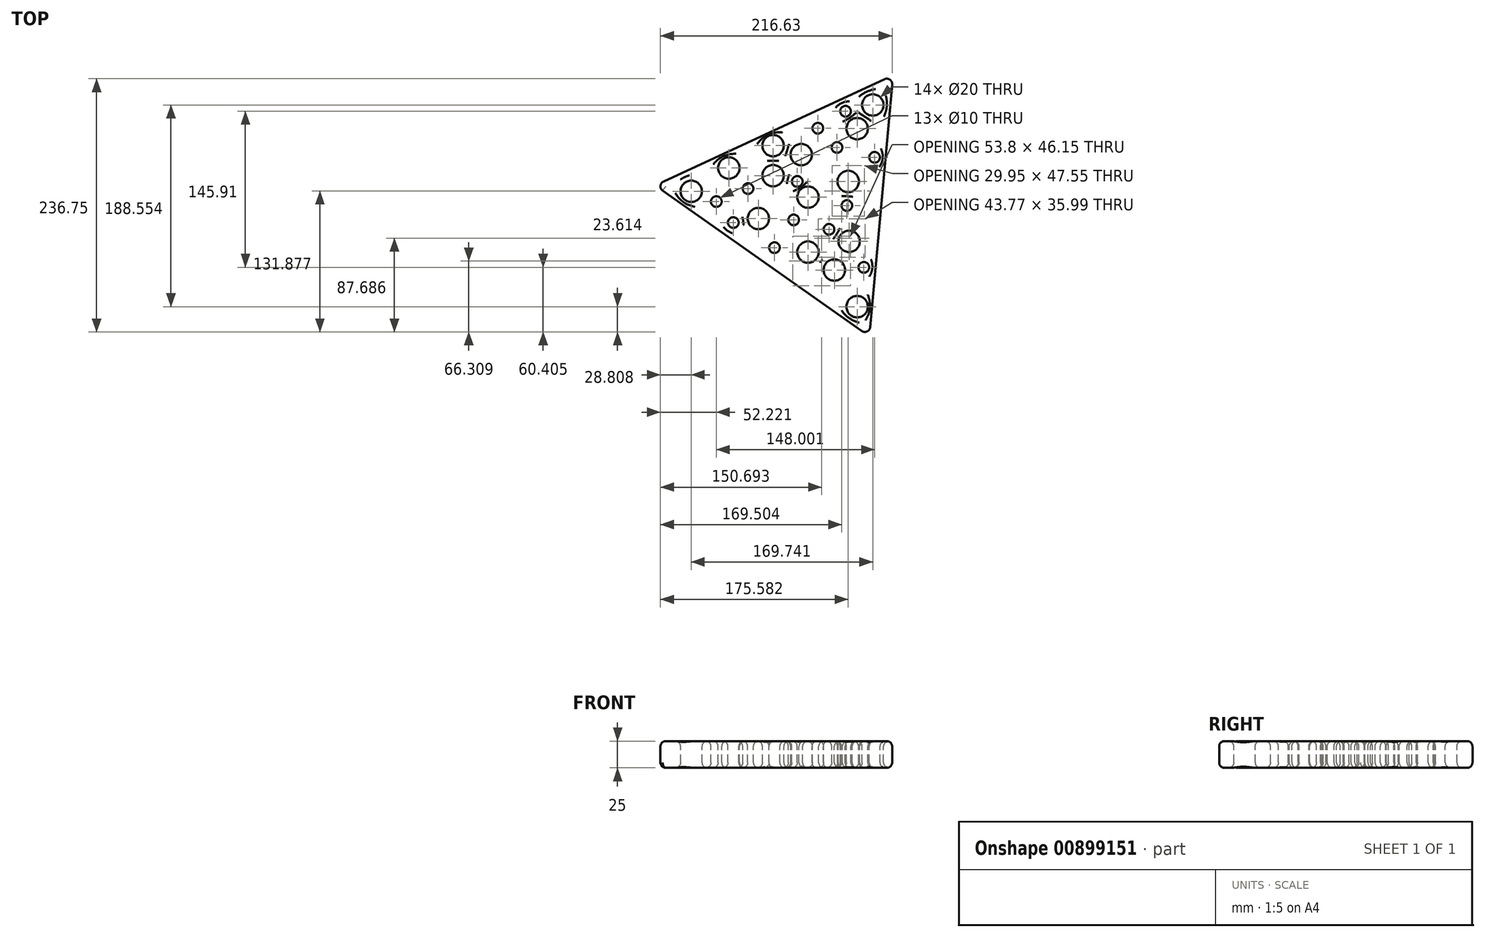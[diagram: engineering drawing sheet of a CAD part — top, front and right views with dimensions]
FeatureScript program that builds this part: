
annotation { "Feature Type Name" : "Feature", "Feature Type Description" : "" }
export const myFeature = defineFeature(function(context is Context, id is Id, definition is map)
    precondition{}
    {
        {
            var Q0;
            Q0=qCreatedBy(makeId("Top.planeOp"),FACE);
            var sketch = newSketch(context, id + "F0", { "sketchPlane" : qUnion([Q0])});
            skLineSegment(sketch, "E0", {"start": v(7.08, -4.99) * mm, "end": v(193.2, -136.12) * mm});
            skLineSegment(sketch, "E1", {"start": v(201.06, -132.48) * mm, "end": v(221.57, 94.27) * mm});
            skLineSegment(sketch, "E2", {"start": v(214.49, 99.26) * mm, "end": v(7.86, 3.64) * mm});
            skPoint(sketch, "E3.visualSharp", {"position": v(0, 0) * mm});
            skArc(sketch, "E3.filletArc", {"start": v(7.86, 3.64) * mm, "mid": v(4.98, -0.45) * mm, "end": v(7.08, -4.99) * mm});
            skPoint(sketch, "E4.visualSharp", {"position": v(222.35, 102.9) * mm});
            skArc(sketch, "E4.filletArc", {"start": v(221.57, 94.27) * mm, "mid": v(219.47, 98.8) * mm, "end": v(214.49, 99.26) * mm});
            skPoint(sketch, "E5.visualSharp", {"position": v(200.28, -141.1) * mm});
            skArc(sketch, "E5.filletArc", {"start": v(193.2, -136.12) * mm, "mid": v(198.18, -136.57) * mm, "end": v(201.06, -132.48) * mm});
            skSolve(sketch);
        }
        {
            var Q0;
            Q0=makeQuery(id+"F0.imprint","IMPRINT",FACE,{"disambiguationData":[TD([[makeQuery(id+"F0.imprint","IMPRINT",EDGE,{"derivedFrom":sQuery(id+"F0.wireOp",EDGE,"E0")}),1.0]])]});
            extrude(context, id + "F1", {"entities" : qUnion([Q0]), "depth" : 25 * mm, "offsetDistance" : 25 * mm});
        }
        {
            var Q0;
            Q0=makeQuery(id+"F1.opExtrude","CAP_FACE",FACE,{"disambiguationData":[OSD([sQuery(id+"F0.wireOp",EDGE,"E0"),sQuery(id+"F0.wireOp",EDGE,"E1"),sQuery(id+"F0.wireOp",EDGE,"E2"),sQuery(id+"F0.wireOp",EDGE,"E3.filletArc"),sQuery(id+"F0.wireOp",EDGE,"E4.filletArc"),sQuery(id+"F0.wireOp",EDGE,"E5.filletArc")])],"isStart":false});
            var sketch = newSketch(context, id + "F2", { "sketchPlane" : qUnion([Q0])});
            skPoint(sketch, "E6", {"position": v(33.77, -5.55) * mm});
            skPoint(sketch, "E7", {"position": v(68.89, 16.19) * mm});
            skPoint(sketch, "E8", {"position": v(96.48, -31.05) * mm});
            skPoint(sketch, "E9", {"position": v(142.89, -10.99) * mm});
            skPoint(sketch, "E10", {"position": v(136.62, 28.73) * mm});
            skPoint(sketch, "E11", {"position": v(188.88, 52.98) * mm});
            skPoint(sketch, "E12", {"position": v(203.5, 75.14) * mm});
            skPoint(sketch, "E13", {"position": v(180.51, 3.64) * mm});
            skPoint(sketch, "E14", {"position": v(110.28, 9.08) * mm});
            skPoint(sketch, "E15", {"position": v(110.28, 37.1) * mm});
            skPoint(sketch, "E16", {"position": v(181.35, -52.38) * mm});
            skPoint(sketch, "E17", {"position": v(142.89, -62.41) * mm});
            skPoint(sketch, "E18", {"position": v(188.88, -113.42) * mm});
            skPoint(sketch, "E19", {"position": v(167.55, -79.13) * mm});
            skSolve(sketch);
        }
        {
            var Q0;
            Q0=sQuery(id+"F2.wireOp",VERTEX,"E7");
            var Q1;
            Q1=sQuery(id+"F2.wireOp",VERTEX,"E14");
            var Q2;
            Q2=sQuery(id+"F2.wireOp",VERTEX,"E10");
            var Q3;
            Q3=sQuery(id+"F2.wireOp",VERTEX,"E12");
            var Q4;
            Q4=sQuery(id+"F2.wireOp",VERTEX,"E18");
            var Q5;
            Q5=sQuery(id+"F2.wireOp",VERTEX,"E16");
            var Q6;
            Q6=sQuery(id+"F2.wireOp",VERTEX,"E8");
            var Q7;
            Q7=sQuery(id+"F2.wireOp",VERTEX,"E13");
            var Q8;
            Q8=sQuery(id+"F2.wireOp",VERTEX,"E6");
            var Q9;
            Q9=sQuery(id+"F2.wireOp",VERTEX,"E15");
            var Q10;
            Q10=sQuery(id+"F2.wireOp",VERTEX,"E17");
            var Q11;
            Q11=sQuery(id+"F2.wireOp",VERTEX,"E19");
            var Q12;
            Q12=sQuery(id+"F2.wireOp",VERTEX,"E9");
            var Q13;
            Q13=sQuery(id+"F2.wireOp",VERTEX,"E11");
            var Q14;
            Q14=makeQuery(id+"F1.opExtrude","SWEPT_BODY",BODY,{"disambiguationData":[OSD([sQuery(id+"F0.wireOp",EDGE,"E0"),sQuery(id+"F0.wireOp",EDGE,"E1"),sQuery(id+"F0.wireOp",EDGE,"E2"),sQuery(id+"F0.wireOp",EDGE,"E3.filletArc"),sQuery(id+"F0.wireOp",EDGE,"E4.filletArc"),sQuery(id+"F0.wireOp",EDGE,"E5.filletArc")])]});
            hole(context, id + "F3", {"style" : HoleStyle.SIMPLE, "endStyle" : HoleEndStyle.THROUGH, "holeDiameter" : 20 * mm, "majorDiameter" : 5 * mm, "isTappedThrough" : true, "tappedDepth" : 12 * mm, "tapClearance" : 3, "locations" : qUnion([Q0, Q1, Q2, Q3, Q4, Q5, Q6, Q7, Q8, Q9, Q10, Q11, Q12, Q13]), "scope" : qUnion([Q14])});
        }
        {
            var Q0;
            Q0=makeQuery(id+"F1.opExtrude","CAP_FACE",FACE,{"disambiguationData":[OSD([sQuery(id+"F0.wireOp",EDGE,"E0"),sQuery(id+"F0.wireOp",EDGE,"E1"),sQuery(id+"F0.wireOp",EDGE,"E2"),sQuery(id+"F0.wireOp",EDGE,"E3.filletArc"),sQuery(id+"F0.wireOp",EDGE,"E4.filletArc"),sQuery(id+"F0.wireOp",EDGE,"E5.filletArc")])],"isStart":false});
            var sketch = newSketch(context, id + "F4", { "sketchPlane" : qUnion([Q0])});
            skPoint(sketch, "E20", {"position": v(152.08, 53.4) * mm});
            skPoint(sketch, "E21", {"position": v(170.06, 35.42) * mm});
            skPoint(sketch, "E22", {"position": v(132.85, 3.64) * mm});
            skPoint(sketch, "E23", {"position": v(86.86, -3.04) * mm});
            skPoint(sketch, "E24", {"position": v(57.18, -15.17) * mm});
            skPoint(sketch, "E25", {"position": v(111.53, -58.23) * mm});
            skPoint(sketch, "E26", {"position": v(129.5, -32.3) * mm});
            skPoint(sketch, "E27", {"position": v(162.54, -41.09) * mm});
            skPoint(sketch, "E28", {"position": v(179.26, -18.93) * mm});
            skPoint(sketch, "E29", {"position": v(195.15, -76.62) * mm});
            skPoint(sketch, "E30", {"position": v(205.18, 26.22) * mm});
            skPoint(sketch, "E31", {"position": v(178, 69.29) * mm});
            skPoint(sketch, "E32", {"position": v(73.07, -34.82) * mm});
            skSolve(sketch);
        }
        {
            var Q0;
            Q0=sQuery(id+"F4.wireOp",VERTEX,"E20");
            var Q1;
            Q1=sQuery(id+"F4.wireOp",VERTEX,"E31");
            var Q2;
            Q2=sQuery(id+"F4.wireOp",VERTEX,"E21");
            var Q3;
            Q3=sQuery(id+"F4.wireOp",VERTEX,"E30");
            var Q4;
            Q4=sQuery(id+"F4.wireOp",VERTEX,"E28");
            var Q5;
            Q5=sQuery(id+"F4.wireOp",VERTEX,"E22");
            var Q6;
            Q6=sQuery(id+"F4.wireOp",VERTEX,"E23");
            var Q7;
            Q7=sQuery(id+"F4.wireOp",VERTEX,"E24");
            var Q8;
            Q8=sQuery(id+"F4.wireOp",VERTEX,"E32");
            var Q9;
            Q9=sQuery(id+"F4.wireOp",VERTEX,"E25");
            var Q10;
            Q10=sQuery(id+"F4.wireOp",VERTEX,"E26");
            var Q11;
            Q11=sQuery(id+"F4.wireOp",VERTEX,"E27");
            var Q12;
            Q12=sQuery(id+"F4.wireOp",VERTEX,"E29");
            var Q13;
            Q13=makeQuery(id+"F1.opExtrude","SWEPT_BODY",BODY,{"disambiguationData":[OSD([sQuery(id+"F0.wireOp",EDGE,"E0"),sQuery(id+"F0.wireOp",EDGE,"E1"),sQuery(id+"F0.wireOp",EDGE,"E2"),sQuery(id+"F0.wireOp",EDGE,"E3.filletArc"),sQuery(id+"F0.wireOp",EDGE,"E4.filletArc"),sQuery(id+"F0.wireOp",EDGE,"E5.filletArc")])]});
            hole(context, id + "F5", {"style" : HoleStyle.SIMPLE, "endStyle" : HoleEndStyle.THROUGH, "holeDiameter" : 10 * mm, "majorDiameter" : 5 * mm, "isTappedThrough" : true, "tappedDepth" : 12 * mm, "tapClearance" : 3, "locations" : qUnion([Q0, Q1, Q2, Q3, Q4, Q5, Q6, Q7, Q8, Q9, Q10, Q11, Q12]), "scope" : qUnion([Q13])});
        }
        {
            var Q0;
            Q0=makeQuery(id+"F1.opExtrude","CAP_FACE",FACE,{"disambiguationData":[OSD([sQuery(id+"F0.wireOp",EDGE,"E0"),sQuery(id+"F0.wireOp",EDGE,"E1"),sQuery(id+"F0.wireOp",EDGE,"E2"),sQuery(id+"F0.wireOp",EDGE,"E3.filletArc"),sQuery(id+"F0.wireOp",EDGE,"E4.filletArc"),sQuery(id+"F0.wireOp",EDGE,"E5.filletArc")])],"isStart":false});
            var Q1;
            Q1=makeQuery(id+"F1.opExtrude","CAP_FACE",FACE,{"disambiguationData":[OSD([sQuery(id+"F0.wireOp",EDGE,"E0"),sQuery(id+"F0.wireOp",EDGE,"E1"),sQuery(id+"F0.wireOp",EDGE,"E2"),sQuery(id+"F0.wireOp",EDGE,"E3.filletArc"),sQuery(id+"F0.wireOp",EDGE,"E4.filletArc"),sQuery(id+"F0.wireOp",EDGE,"E5.filletArc")])],"isStart":true});
            fillet(context, id + "F6", {"entities" : qUnion([Q0, Q1]), "radius" : 5 * mm, "tangentPropagation" : true, "allowEdgeOverflow" : false});
        }
    });
